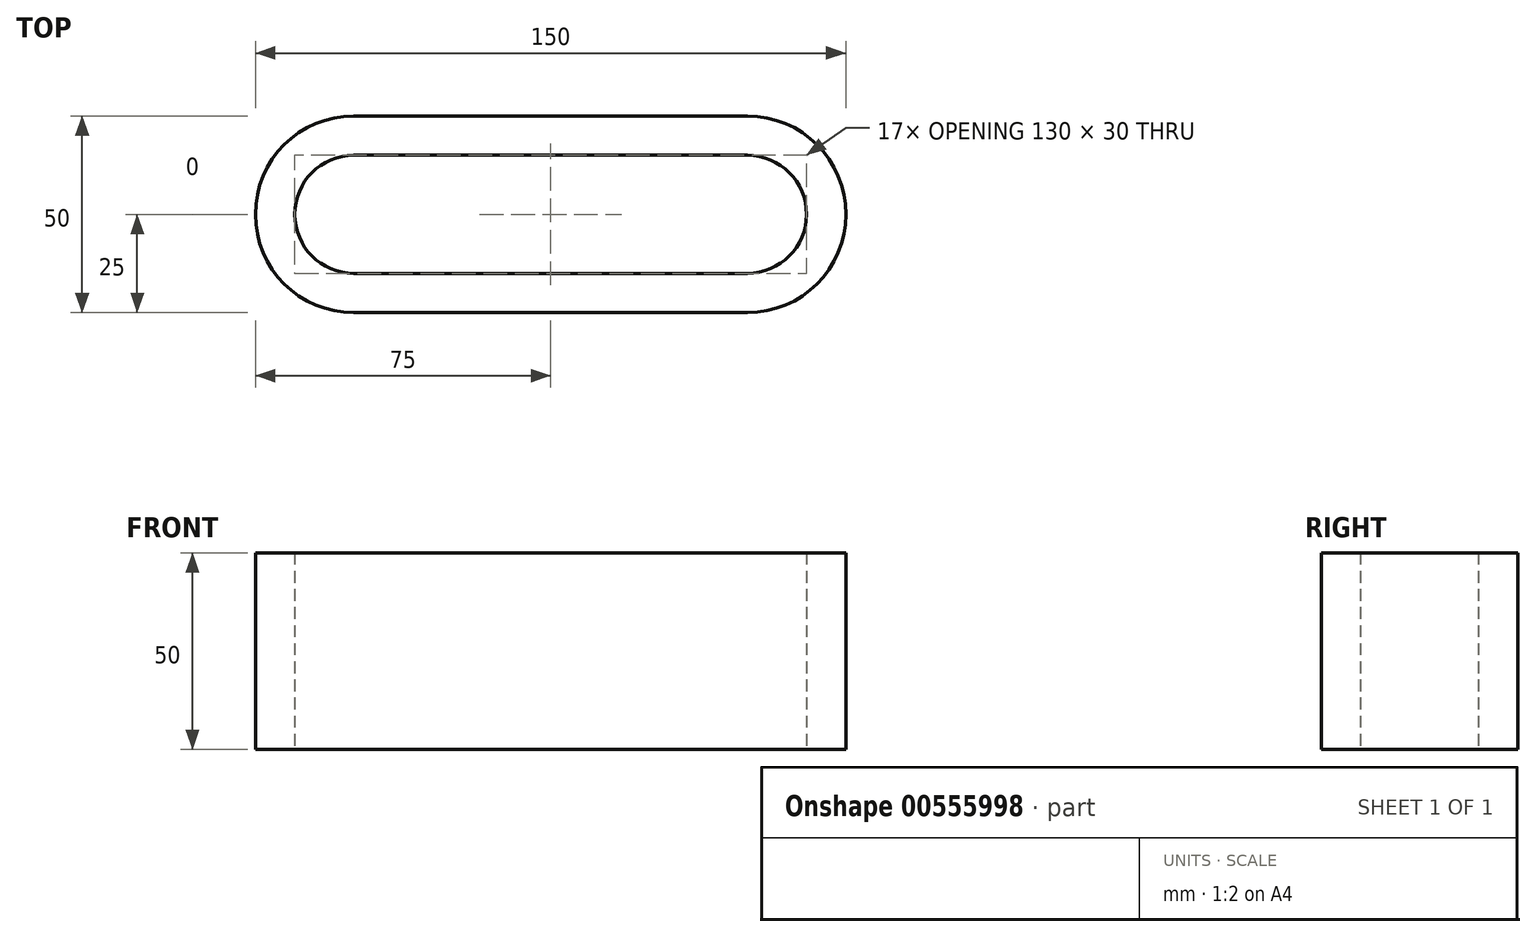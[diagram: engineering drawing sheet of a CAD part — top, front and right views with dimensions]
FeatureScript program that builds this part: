
annotation { "Feature Type Name" : "Feature", "Feature Type Description" : "" }
export const myFeature = defineFeature(function(context is Context, id is Id, definition is map)
    precondition{}
    {
        {
            var Q0;
            Q0=qCreatedBy(makeId("Top.planeOp"),FACE);
            var sketch = newSketch(context, id + "F0", { "sketchPlane" : qUnion([Q0])});
            skArc(sketch, "E0", {"start": v(0, 25) * mm, "mid": v(-25, 0) * mm, "end": v(0, -25) * mm});
            skLineSegment(sketch, "E1.bottom", {"start": v(0, 25) * mm, "end": v(50, 25) * mm});
            skLineSegment(sketch, "E1.top", {"start": v(0, -25) * mm, "end": v(50, -25) * mm});
            skLineSegment(sketch, "E1.right", {"start": v(50, 25) * mm, "end": v(50, -25) * mm, "construction": true});
            skLineSegment(sketch, "E2.MirrorCS", {"start": v(100, 25) * mm, "end": v(50, 25) * mm});
            skArc(sketch, "E3.MirrorCS", {"start": v(100, 25) * mm, "mid": v(125, 0) * mm, "end": v(100, -25) * mm});
            skLineSegment(sketch, "E4.MirrorCS", {"start": v(100, -25) * mm, "end": v(50, -25) * mm});
            skArc(sketch, "E5.0", {"start": v(0, 15) * mm, "mid": v(-15, 0) * mm, "end": v(0, -15) * mm});
            skLineSegment(sketch, "E5.1", {"start": v(100, 15) * mm, "end": v(50, 15) * mm});
            skArc(sketch, "E5.2", {"start": v(100, 15) * mm, "mid": v(115, 0) * mm, "end": v(100, -15) * mm});
            skLineSegment(sketch, "E5.3", {"start": v(0, 15) * mm, "end": v(50, 15) * mm});
            skLineSegment(sketch, "E5.4", {"start": v(100, -15) * mm, "end": v(50, -15) * mm});
            skLineSegment(sketch, "E5.5", {"start": v(0, -15) * mm, "end": v(50, -15) * mm});
            skSolve(sketch);
        }
        {
            var Q0;
            Q0 = qSketchRegion(id + "F0", true);
            extrude(context, id + "F1", {"entities" : qUnion([Q0]), "depth" : 50 * mm, "offsetDistance" : 25 * mm});
        }
    });
